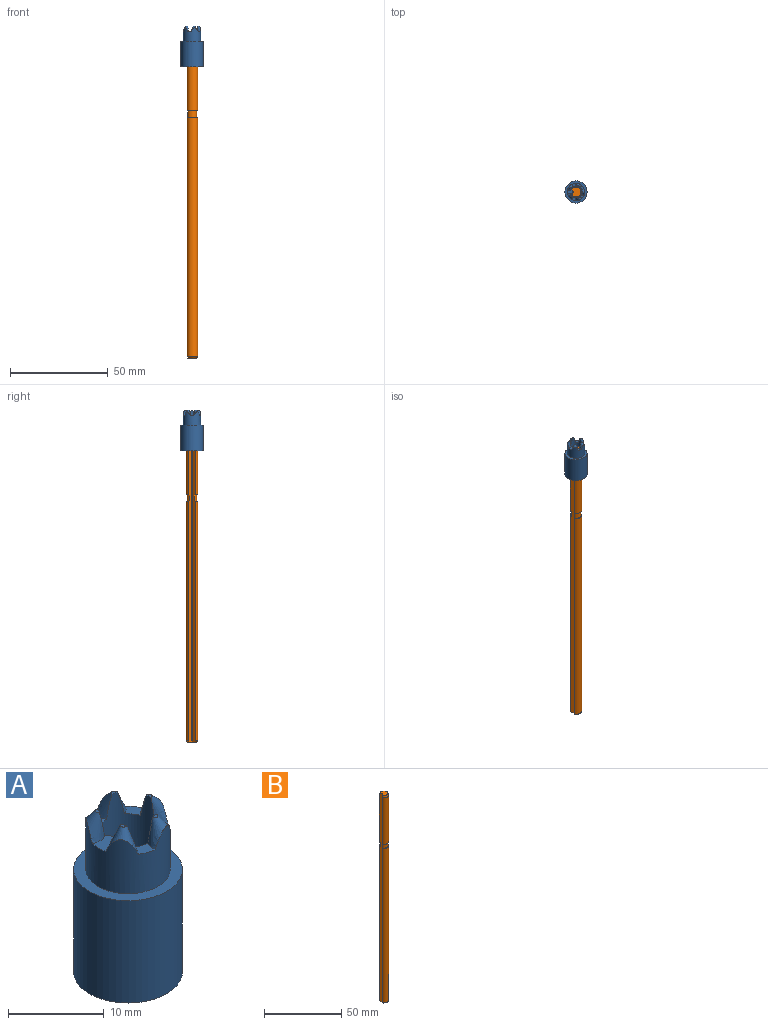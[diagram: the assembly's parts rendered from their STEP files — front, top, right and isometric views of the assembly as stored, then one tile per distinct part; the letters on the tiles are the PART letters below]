
ASSEMBLY  parts=2 mates=1
PART A: 25 faces, bbox 11.7x11.7x21.3 mm
  f0: cone r=1.8mm half-angle=24.8deg, axis (0.34,0,-0.94), area 9mm2, adj f1,f2,f3,f4,f21
  f1: plane 0.97x0.71mm, normal (0,0,1), area 0.2mm2, adj f0,f2
  f2: cylinder r=3.06mm len=20.85mm, axis (0,0,-1), area 308.4mm2, adj f0,f1,f4,f5,f6,f7,f8,f9
  f3: cylinder r=4.4mm len=8.8mm, axis (0,0,-1), area 159.2mm2, adj f0,f4,f6,f7,f11,f12,f16,f17
  f4: plane 2.32x2.22mm, normal (0,0,1), area 2.2mm2, adj f0,f2,f3,f6
  f5: plane 0.97x0.81mm, normal (0,0,1), area 0.2mm2, adj f2,f6
  f6: cone r=1.8mm half-angle=24.8deg, axis (0.11,0.33,-0.94), area 9mm2, adj f2,f3,f4,f5,f7
  f7: plane 2.2x1.91mm, normal (0,0,1), area 2.2mm2, adj f2,f3,f6,f11
  f8: plane 0.63x0.58mm, normal (0,0,1), area 0.2mm2, adj f2,f11
  f9: cylinder r=0.15mm len=20.77mm, axis (0,0,-1), area 4mm2, adj f2,f10,f11,f23
  f10: plane 20.17x0.68mm, normal (0.71,0.71,0), area 17.7mm2, adj f9,f11,f12,f20,f23
  f11: cone r=1.8mm half-angle=24.8deg, axis (-0.28,0.2,-0.94), area 9.8mm2, adj f2,f3,f7,f8,f9,f10,f12
  f12: plane 2.7x2.17mm, normal (0,0,1), area 4.4mm2, adj f3,f10,f11,f14,f16,f20
  f13: plane 0.63x0.58mm, normal (0,0,1), area 0.2mm2, adj f2,f16
  f14: plane 20.17x0.68mm, normal (0.71,-0.71,0), area 17.7mm2, adj f12,f15,f16,f20,f23
  f15: cylinder r=0.15mm len=20.77mm, axis (0,0,-1), area 4mm2, adj f2,f14,f16,f23
  f16: cone r=1.8mm half-angle=24.8deg, axis (-0.28,-0.2,-0.94), area 9.8mm2, adj f2,f3,f12,f13,f14,f15,f17
  f17: plane 2.2x1.91mm, normal (0,0,1), area 2.2mm2, adj f2,f3,f16,f18
  f18: cone r=1.8mm half-angle=24.8deg, axis (0.11,-0.33,-0.94), area 9mm2, adj f2,f3,f17,f19,f21
  f19: plane 0.97x0.81mm, normal (0,0,1), area 0.2mm2, adj f2,f18
  f20: cylinder r=0.9mm len=17.97mm, axis (0,0,-1), area 25.4mm2, adj f10,f12,f14,f23
  f21: plane 2.32x2.22mm, normal (0,0,1), area 2.2mm2, adj f0,f2,f3,f18
  f22: cylinder r=5.68mm len=13.05mm, axis (0,0,1), area 465.3mm2, adj f23,f24
  f23: plane 11.35x11.35mm, normal (0,0,-1), area 74.2mm2, adj f2,f9,f10,f14,f15,f20,f22
  f24: plane 11.35x11.35mm, normal (0,0,1), area 40.4mm2, adj f3,f22
PART B: 12 faces, bbox 5.6x5.9x165 mm
  f0: cylinder r=2.95mm len=122.55mm, axis (0,0,-1), area 1867.7mm2, adj f1,f3,f7,f11
  f1: plane 165.02x1.36mm, normal (-0.71,0.71,0), area 309.7mm2, adj f0,f2,f4,f5,f6,f7,f8,f9
  f2: cylinder r=2.95mm len=37.05mm, axis (0,0,-1), area 564.7mm2, adj f1,f3,f8,f10
  f3: plane 165.02x1.36mm, normal (-0.71,-0.71,0), area 309.7mm2, adj f0,f2,f4,f5,f6,f7,f8,f9
  f4: cylinder r=0.3mm len=165mm, axis (0,0,-1), area 77.8mm2, adj f1,f3,f5,f6
  f5: plane 5.09x4.75mm, normal (0,0,1), area 18.2mm2, adj f1,f3,f4,f8
  f6: plane 4.69x4.41mm, normal (0,0,-1), area 15.6mm2, adj f1,f3,f4,f7
  f7: cone r=2.95mm half-angle=45deg, axis (0,0,1), area 11.7mm2, adj f0,f1,f3,f6
  f8: cone r=2.54mm half-angle=15deg, axis (0,0,-1), area 22.2mm2, adj f1,f2,f3,f5
  f9: cylinder r=2.4mm len=4.8mm, axis (0,0,-1), area 41.8mm2, adj f1,f3,f10,f11
  f10: plane 5.89x5.45mm, normal (0,0,-1), area 7.6mm2, adj f1,f2,f3,f9
  f11: plane 5.89x5.45mm, normal (0,0,1), area 7.6mm2, adj f0,f1,f3,f9
PLACE A at identity fixed
PLACE B t=(0,0,-162.15)mm
MATE fastened B.f0 <-> A.f2  axis (0,0,1) through (0,0,2.85)mm
